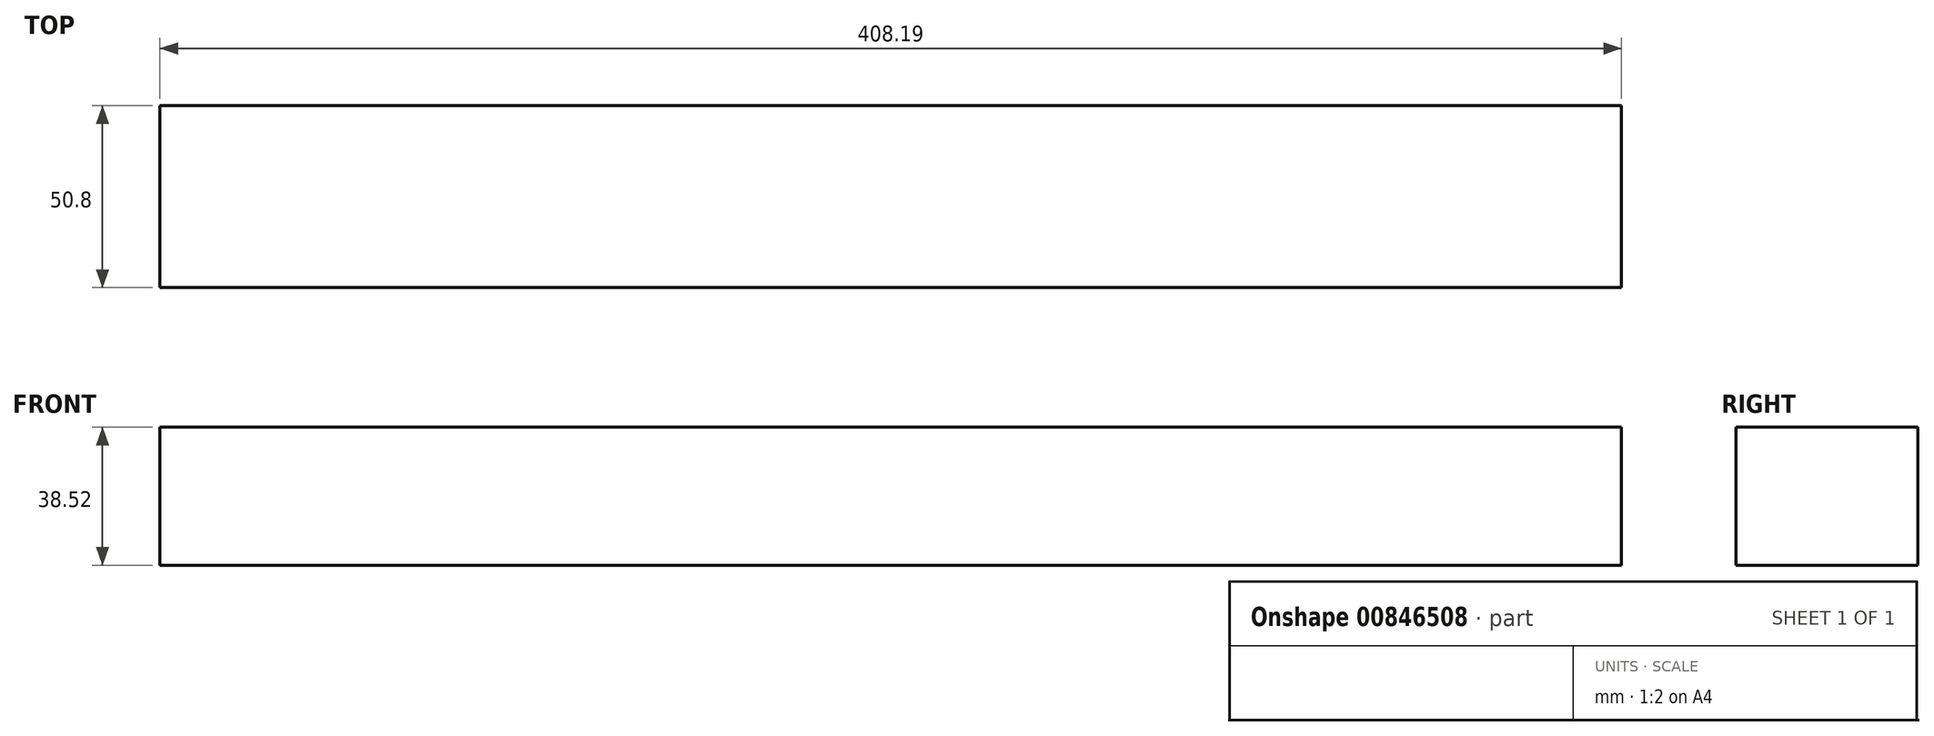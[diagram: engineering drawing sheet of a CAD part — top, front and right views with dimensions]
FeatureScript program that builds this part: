
annotation { "Feature Type Name" : "Feature", "Feature Type Description" : "" }
export const myFeature = defineFeature(function(context is Context, id is Id, definition is map)
    precondition{}
    {
        {
            var Q0;
            Q0=qCreatedBy(makeId("Front.planeOp"),FACE);
            var sketch = newSketch(context, id + "F0", { "sketchPlane" : qUnion([Q0])});
            skLineSegment(sketch, "E0", {"start": v(0, 0) * mm, "end": v(-408.2, 0) * mm});
            skLineSegment(sketch, "E1", {"start": v(-408.2, 0) * mm, "end": v(-408.2, 38.52) * mm});
            skLineSegment(sketch, "E2", {"start": v(-408.2, 38.52) * mm, "end": v(0, 38.52) * mm});
            skLineSegment(sketch, "E3", {"start": v(0, 38.52) * mm, "end": v(0, 0) * mm});
            skSolve(sketch);
        }
        {
            var Q0;
            Q0 = qSketchRegion(id + "F0", true);
            extrude(context, id + "F1", {"entities" : qUnion([Q0]), "depth" : 50.8 * mm, "offsetDistance" : 25.4 * mm});
        }
    });
